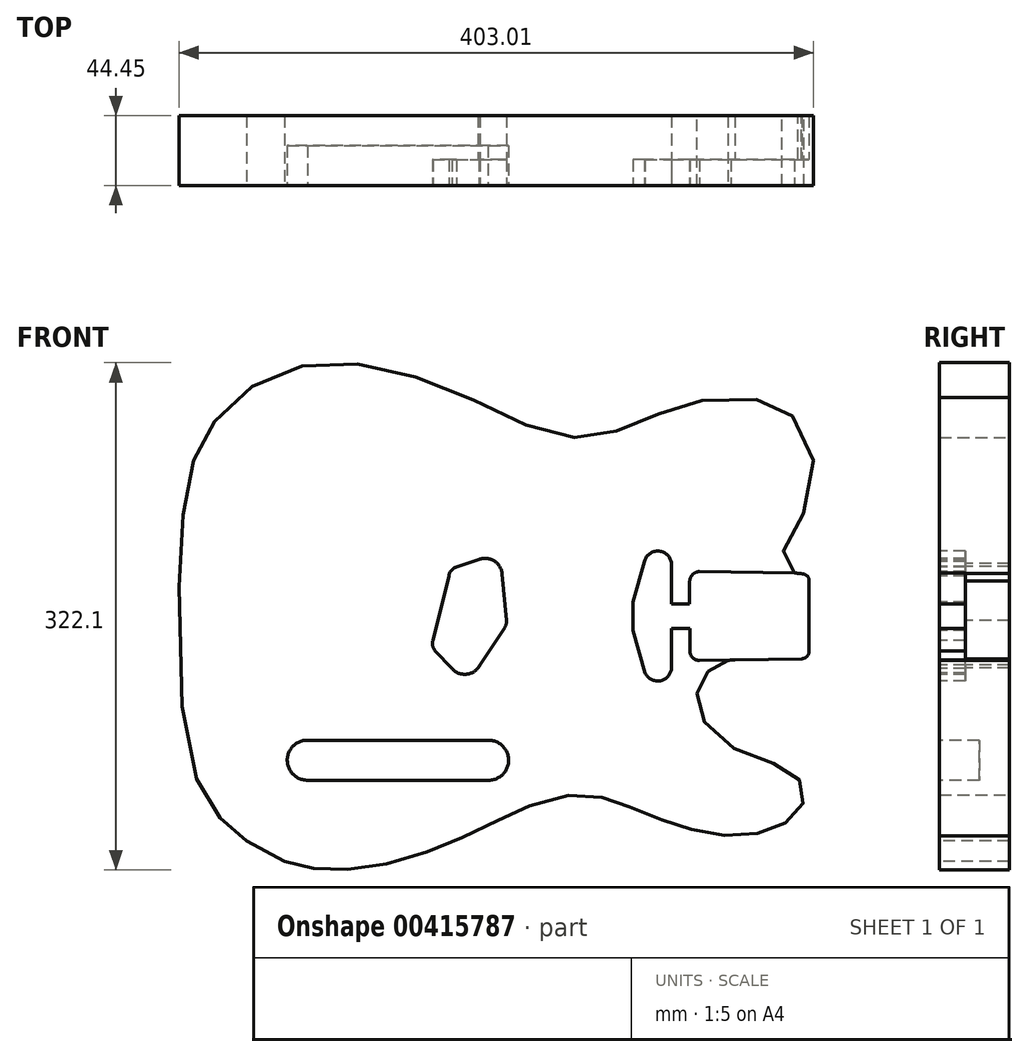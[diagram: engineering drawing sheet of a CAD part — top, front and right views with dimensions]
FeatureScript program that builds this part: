
annotation { "Feature Type Name" : "Feature", "Feature Type Description" : "" }
export const myFeature = defineFeature(function(context is Context, id is Id, definition is map)
    precondition{}
    {
        {
            var Q0;
            Q0=qCreatedBy(makeId("Front.planeOp"),FACE);
            var sketch = newSketch(context, id + "F0", { "sketchPlane" : qUnion([Q0])});
            skLineSegment(sketch, "E0", {"start": v(-516.67, 18.61) * mm, "end": v(321.18, 18.61) * mm, "construction": true});
            skArc(sketch, "E1", {"start": v(-128.34, -85.7) * mm, "mid": v(-115.64, -72.78) * mm, "end": v(-128.8, -60.31) * mm});
            skArc(sketch, "E2", {"start": v(-243.5, -60.3) * mm, "mid": v(-256.2, -73.12) * mm, "end": v(-243.25, -85.7) * mm});
            skLineSegment(sketch, "E3", {"start": v(-243.25, -85.7) * mm, "end": v(-128.34, -85.7) * mm});
            skLineSegment(sketch, "E4", {"start": v(-128.8, -60.31) * mm, "end": v(-243.5, -60.3) * mm});
            skPoint(sketch, "E5", {"position": v(52.33, 18.61) * mm});
            skArc(sketch, "E6", {"start": v(-119.69, 45.36) * mm, "mid": v(-124.7, 53.58) * mm, "end": v(-134.28, 54.63) * mm});
            skArc(sketch, "E7", {"start": v(-148.83, 49.75) * mm, "mid": v(-151.98, 47.66) * mm, "end": v(-153.51, 44.2) * mm});
            skArc(sketch, "E8", {"start": v(-163.76, 3.13) * mm, "mid": v(-163.89, -0.38) * mm, "end": v(-162.23, -3.47) * mm});
            skLineSegment(sketch, "E9", {"start": v(-163.76, 3.13) * mm, "end": v(-153.51, 44.2) * mm});
            skLineSegment(sketch, "E10", {"start": v(-148.83, 49.75) * mm, "end": v(-134.28, 54.63) * mm});
            skArc(sketch, "E11", {"start": v(-118.05, 11.43) * mm, "mid": v(-117.14, 13.51) * mm, "end": v(-116.97, 15.78) * mm});
            skLineSegment(sketch, "E12", {"start": v(-135.1, -14.47) * mm, "end": v(-118.05, 11.43) * mm});
            skLineSegment(sketch, "E13", {"start": v(-116.96, 15.7) * mm, "end": v(-119.69, 45.36) * mm});
            skLineSegment(sketch, "E14", {"start": v(-151.67, -14.69) * mm, "end": v(-162.5, -3.18) * mm});
            skArc(sketch, "E15.trimOffspring", {"start": v(-151.67, -14.69) * mm, "mid": v(-142.09, -18.3) * mm, "end": v(-133.73, -12.4) * mm});
            skLineSegment(sketch, "E16", {"start": v(-194.71, 45.6) * mm, "end": v(-194.72, -21.39) * mm});
            skPoint(sketch, "E17", {"position": v(-194.72, -8.38) * mm});
            skPoint(sketch, "E18", {"position": v(-194.72, 2.42) * mm});
            skPoint(sketch, "E19", {"position": v(-194.72, 13.21) * mm});
            skPoint(sketch, "E20", {"position": v(-194.71, 24) * mm});
            skPoint(sketch, "E21", {"position": v(-194.71, 34.8) * mm});
            skPoint(sketch, "E22", {"position": v(-194.71, 45.6) * mm});
            skLineSegment(sketch, "E23", {"start": v(-36.46, 27.65) * mm, "end": v(-36.46, 9.57) * mm});
            skArc(sketch, "E24", {"start": v(-28.88, -17.42) * mm, "mid": v(-19.11, -22.48) * mm, "end": v(-12.18, -13.95) * mm});
            skArc(sketch, "E25", {"start": v(-12.21, 50.2) * mm, "mid": v(-19.3, 59.75) * mm, "end": v(-29.32, 53.3) * mm});
            skLineSegment(sketch, "E26", {"start": v(-28.88, -17.42) * mm, "end": v(-36.46, 9.57) * mm});
            skLineSegment(sketch, "E27", {"start": v(-12.21, 52.17) * mm, "end": v(-12.18, -13.95) * mm});
            skLineSegment(sketch, "E28", {"start": v(-29.32, 53.3) * mm, "end": v(-36.46, 27.65) * mm});
            skLineSegment(sketch, "E29", {"start": v(-258.04, -137.13) * mm, "end": v(-282.06, -124.31) * mm});
            skFitSpline(sketch, "E30", {"points": [v(70.3, 45.52) * mm, v(65.71, 46.13) * mm, v(62.08, 47.64) * mm, v(59.02, 50.94) * mm, v(58.1, 53.39) * mm, v(57.86, 55.85) * mm, v(58.15, 57.83) * mm, v(58.96, 59.94) * mm, v(61.7, 64.24) * mm, v(64.7, 69.4) * mm, v(66.85, 73.47) * mm, v(71.82, 84.43) * mm, v(75.3, 95.03) * mm, v(76.91, 102.5) * mm, v(77.87, 117.11) * mm, v(74.22, 132.27) * mm, v(69.05, 141.27) * mm, v(65.97, 144.7) * mm, v(63.88, 146.4) * mm, v(62.12, 147.7) * mm, v(59.64, 149.34) * mm, v(54.9, 151.92) * mm, v(43.32, 155.68) * mm, v(32.06, 157.3) * mm, v(17.27, 157.27) * mm, v(8.59, 155.95) * mm, v(-0.59, 153.71) * mm, v(-9.07, 151.17) * mm, v(-14.49, 149.29) * mm, v(-22.45, 146.25) * mm, v(-30.28, 142.93) * mm, v(-39.25, 139.32) * mm, v(-44.98, 136.91) * mm, v(-51.03, 134.84) * mm, v(-57.4, 133.34) * mm, v(-64.53, 132.27) * mm, v(-72.04, 131.97) * mm, v(-80.81, 132.86) * mm, v(-89.38, 134.69) * mm, v(-99.36, 137.9) * mm, v(-109.86, 142.33) * mm, v(-121.04, 147.42) * mm, v(-134.7, 154.26) * mm, v(-143.63, 158.41) * mm, v(-157.48, 164.22) * mm, v(-175.06, 170.7) * mm, v(-186.61, 174.2) * mm, v(-200.65, 177.23) * mm, v(-215.54, 179.1) * mm, v(-230.39, 179.44) * mm, v(-239.57, 178.67) * mm, v(-249.54, 176.82) * mm, v(-258.34, 174.21) * mm, v(-270, 169.29) * mm, v(-280.98, 162.7) * mm, v(-288.67, 156.78) * mm, v(-296.44, 149.34) * mm, v(-303.1, 141.38) * mm, v(-307.9, 134.31) * mm, v(-310.98, 128.7) * mm, v(-314.13, 121.24) * mm, v(-316.57, 114.28) * mm, v(-319.25, 104.1) * mm, v(-321.3, 91) * mm, v(-323.1, 75.63) * mm, v(-324.3, 57) * mm, v(-324.88, 31.53) * mm, v(-324.1, -26.04) * mm, v(-319.39, -66.59) * mm, v(-316.7, -76.96) * mm, v(-311.5, -90.72) * mm, v(-307.1, -98.6) * mm, v(-303.5, -103.85) * mm, v(-299.76, -108.6) * mm, v(-295.88, -113) * mm, v(-290.52, -118.18) * mm, v(-287.64, -120.66) * mm, v(-285.35, -122.35) * mm, v(-282.06, -124.31) * mm], "startDerivative": vector(-521.4, 51.1) * mm, "endDerivative": vector(7.82, -3.84) * mm});
            skFitSpline(sketch, "E31", {"points": [v(-258.04, -137.13) * mm, v(-254.56, -138.55) * mm, v(-248.27, -140.28) * mm, v(-242.3, -141.43) * mm, v(-236.22, -142.19) * mm, v(-230.2, -142.56) * mm, v(-222.2, -142.51) * mm, v(-213.36, -141.96) * mm, v(-204.12, -140.83) * mm, v(-193.84, -139.03) * mm, v(-183.73, -136.5) * mm, v(-170.61, -132.2) * mm, v(-165.06, -130.2) * mm, v(-153.97, -125.86) * mm, v(-146.87, -122.89) * mm, v(-137.16, -118.51) * mm, v(-128.9, -114.5) * mm, v(-121.59, -110.71) * mm, v(-115.68, -108) * mm, v(-108.14, -104.67) * mm, v(-101.08, -101.6) * mm, v(-90.11, -97.91) * mm, v(-79.65, -95.76) * mm, v(-75.23, -95.16) * mm, v(-67.68, -95.13) * mm, v(-60.22, -95.91) * mm, v(-52.78, -97.44) * mm, v(-48.12, -98.84) * mm, v(-43.87, -100.4) * mm, v(-38.87, -102.54) * mm, v(-34.86, -104.16) * mm, v(-30.2, -106.05) * mm, v(-19.16, -110.63) * mm, v(-14.29, -112.45) * mm, v(-9.32, -114.16) * mm, v(-2.8, -116.16) * mm, v(4.47, -118.07) * mm, v(10.97, -119.47) * mm, v(18.56, -120.52) * mm, v(24.6, -120.86) * mm, v(29.5, -120.78) * mm, v(37.08, -120.2) * mm, v(45.04, -118.84) * mm, v(49.91, -117.62) * mm, v(54.94, -115.61) * mm, v(59.99, -112.9) * mm, v(65.17, -109.17) * mm, v(68.24, -106.38) * mm, v(70.42, -102.89) * mm, v(71.46, -100.24) * mm, v(71.93, -97.55) * mm, v(72, -94.13) * mm, v(71.54, -91.1) * mm, v(69.6, -86.34) * mm, v(67.2, -83.08) * mm, v(63.48, -79.97) * mm, v(56.62, -76.25) * mm, v(48.22, -73.68) * mm, v(34.67, -69.13) * mm, v(27.1, -65.44) * mm, v(18.7, -59.73) * mm, v(10.23, -51.15) * mm, v(7.82, -47.15) * mm, v(5.3, -41.16) * mm, v(3.95, -34.56) * mm, v(4.02, -30.54) * mm, v(5.12, -25.25) * mm, v(6.55, -21.68) * mm, v(8.68, -18.6) * mm, v(10.8, -16.63) * mm, v(14.31, -14.6) * mm, v(17.92, -12.75) * mm, v(21.08, -10.92) * mm, v(23.17, -9.84) * mm, v(23.76, -9.63) * mm], "startDerivative": vector(304.37, -136.53) * mm, "endDerivative": vector(239.1, 54.76) * mm});
            skPoint(sketch, "E32", {"position": v(5.74, 18.61) * mm});
            skPoint(sketch, "E33", {"position": v(70.3, 18.61) * mm});
            skFitSpline(sketch, "E34", {"points": [v(23.76, -9.63) * mm, v(26.1, -9.26) * mm, v(28.15, -9.2) * mm], "startDerivative": vector(4.61, 1.14) * mm, "endDerivative": vector(5.5, -0.1) * mm});
            skLineSegment(sketch, "E35", {"start": v(28.15, -9.2) * mm, "end": v(70.8, -8.49) * mm});
            skFitSpline(sketch, "E36", {"points": [v(70.8, -8.49) * mm, v(72.08, -8.21) * mm, v(73.2, -7.69) * mm, v(74.06, -6.92) * mm, v(74.58, -6.18) * mm, v(74.92, -5.48) * mm, v(75.1, -4.73) * mm, v(75.17, -3.82) * mm, v(75.18, -2.64) * mm], "startDerivative": vector(9.23, 1.6) * mm, "endDerivative": vector(0.01, 9.01) * mm});
            skLineSegment(sketch, "E37", {"start": v(75.18, -2.64) * mm, "end": v(75.18, 40.91) * mm});
            skFitSpline(sketch, "E38", {"points": [v(75.18, 40.91) * mm, v(75.07, 41.9) * mm, v(74.69, 43.14) * mm, v(73.69, 44.36) * mm, v(72.51, 45.09) * mm, v(71.53, 45.35) * mm, v(70.3, 45.52) * mm], "startDerivative": vector(-0.5, 6.5) * mm, "endDerivative": vector(-7.65, 0.9) * mm});
            skLineSegment(sketch, "E39", {"start": v(5.74, 46.86) * mm, "end": v(5.74, -9.63) * mm});
            skLineSegment(sketch, "E40", {"start": v(99.97, -8.07) * mm, "end": v(99.97, 45.67) * mm});
            skLineSegment(sketch, "E41", {"start": v(99.97, 45.67) * mm, "end": v(5.74, 46.86) * mm});
            skLineSegment(sketch, "E42", {"start": v(-0.61, 40.46) * mm, "end": v(-0.6, 26.31) * mm});
            skLineSegment(sketch, "E43", {"start": v(-12.2, 10.66) * mm, "end": v(-0.6, 10.67) * mm});
            skLineSegment(sketch, "E44", {"start": v(-0.6, 26.31) * mm, "end": v(-12.2, 26.3) * mm});
            skLineSegment(sketch, "E45.trimOffspring", {"start": v(-0.6, 10.67) * mm, "end": v(-0.59, -3.6) * mm});
            skArc(sketch, "E46", {"start": v(-0.59, -3.6) * mm, "mid": v(1.37, -7.88) * mm, "end": v(5.74, -9.63) * mm});
            skArc(sketch, "E47", {"start": v(5.74, 46.86) * mm, "mid": v(1.23, 44.98) * mm, "end": v(-0.61, 40.46) * mm});
            skPoint(sketch, "E48.orphan", {"position": v(-0.62, 51.17) * mm});
            skLineSegment(sketch, "E49", {"start": v(5.74, -9.63) * mm, "end": v(99.97, -8.07) * mm});
            skFitSpline(sketch, "E50", {"points": [v(66.45, 45.99) * mm, v(68.72, 45.67) * mm, v(70.3, 45.52) * mm], "startDerivative": vector(4.35, -0.64) * mm, "endDerivative": vector(3.33, -0.29) * mm});
            skSolve(sketch);
        }
        {
            var Q0;
            {var subQ14=sQuery(id+"F0.wireOp",EDGE,"E6");Q0=makeQuery(id+"F0.imprint","IMPRINT",FACE,{"disambiguationData":[TD([[makeQuery(id+"F0.imprint","IMPRINT",EDGE,{"derivedFrom":subQ14}),-1.0]])]});}
            var Q1;
            {var subQ0=sQuery(id+"F0.wireOp",EDGE,"E35");Q1=makeQuery(id+"F0.imprint","IMPRINT",FACE,{"disambiguationData":[TD([[makeQuery(id+"F0.imprint","IMPRINT",EDGE,{"derivedFrom":subQ0}),1.0]])]});}
            var Q2;
            Q2=makeQuery(id+"F0.imprint","IMPRINT",FACE,{"disambiguationData":[TD([[makeQuery(id+"F0.imprint","IMPRINT",EDGE,{"derivedFrom":sQuery(id+"F0.wireOp",EDGE,"E39")}),-1.0]])]});
            var Q3;
            Q3=makeQuery(id+"F0.imprint","IMPRINT",FACE,{"disambiguationData":[TD([[makeQuery(id+"F0.imprint","IMPRINT",EDGE,{"derivedFrom":sQuery(id+"F0.wireOp",EDGE,"E23")}),1.0]])]});
            var Q4;
            {var subQ8=sQuery(id+"F0.wireOp",EDGE,"E6");Q4=makeQuery(id+"F0.imprint","IMPRINT",FACE,{"disambiguationData":[TD([[makeQuery(id+"F0.imprint","IMPRINT",EDGE,{"derivedFrom":subQ8}),1.0]])]});}
            var Q5;
            {var subQ0=sQuery(id+"F0.wireOp",EDGE,"E3");var subQ6=sQuery(id+"F0.wireOp",EDGE,"E1");var subQ7=makeQuery(id+"F0.imprint","INTERSECT",VERTEX,{"derivedFrom":[subQ6,subQ0]});Q5=makeQuery(id+"F0.imprint","IMPRINT",FACE,{"disambiguationData":[TD([[makeQuery(id+"F0.imprint","IMPRINT",EDGE,{"disambiguationData":[TD([[subQ7,-1.0]])],"derivedFrom":subQ6}),1.0]])]});}
            extrude(context, id + "F1", {"entities" : qUnion([Q0, Q1, Q2, Q3, Q4, Q5]), "oppositeDirection" : true, "depth" : 44.45 * mm});
        }
        {
            var Q0;
            Q0=makeQuery(id+"F0.imprint","IMPRINT",FACE,{"disambiguationData":[TD([[makeQuery(id+"F0.imprint","IMPRINT",EDGE,{"derivedFrom":sQuery(id+"F0.wireOp",EDGE,"E23")}),1.0]])]});
            var Q1;
            {var subQ1=sQuery(id+"F0.wireOp",EDGE,"E6");Q1=makeQuery(id+"F0.imprint","IMPRINT",FACE,{"disambiguationData":[TD([[makeQuery(id+"F0.imprint","IMPRINT",EDGE,{"derivedFrom":subQ1}),1.0]])]});}
            var Q2;
            {var subQ0=sQuery(id+"F0.wireOp",EDGE,"E35");Q2=makeQuery(id+"F0.imprint","IMPRINT",FACE,{"disambiguationData":[TD([[makeQuery(id+"F0.imprint","IMPRINT",EDGE,{"derivedFrom":subQ0}),1.0]])]});}
            var Q3;
            Q3=makeQuery(id+"F0.imprint","IMPRINT",FACE,{"disambiguationData":[TD([[makeQuery(id+"F0.imprint","IMPRINT",EDGE,{"derivedFrom":sQuery(id+"F0.wireOp",EDGE,"E39")}),-1.0]])]});
            extrude(context, id + "F2", {"entities" : qUnion([Q0, Q1, Q2, Q3]), "operationType" : NewBodyOperationType.REMOVE, "oppositeDirection" : true, "depth" : 16.5 * mm});
        }
        {
            var Q0;
            {var subQ0=sQuery(id+"F0.wireOp",EDGE,"E3");var subQ6=sQuery(id+"F0.wireOp",EDGE,"E1");var subQ7=makeQuery(id+"F0.imprint","INTERSECT",VERTEX,{"derivedFrom":[subQ6,subQ0]});Q0=makeQuery(id+"F0.imprint","IMPRINT",FACE,{"disambiguationData":[TD([[makeQuery(id+"F0.imprint","IMPRINT",EDGE,{"disambiguationData":[TD([[subQ7,-1.0]])],"derivedFrom":subQ6}),1.0]])]});}
            var Q1;
            Q1 = qSketchRegion(id + "FKxfrQYo5yUS65J_1", true);
            extrude(context, id + "F3", {"entities" : qUnion([Q0, Q1]), "operationType" : NewBodyOperationType.REMOVE, "oppositeDirection" : true, "depth" : 25.4 * mm});
        }
    });
